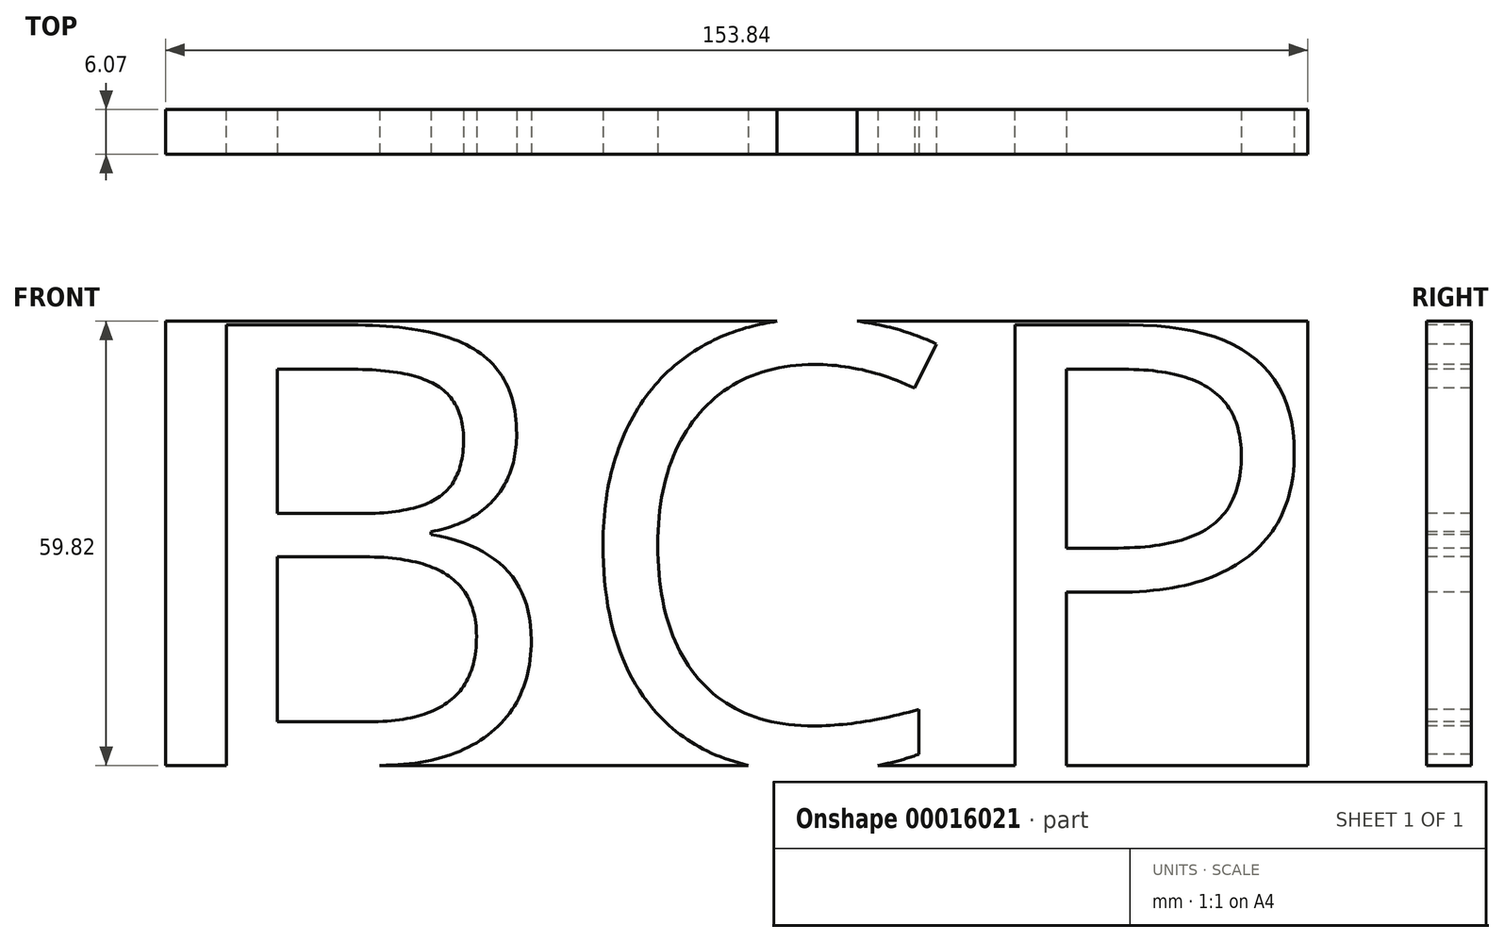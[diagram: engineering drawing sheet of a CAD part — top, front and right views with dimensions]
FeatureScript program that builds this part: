
annotation { "Feature Type Name" : "Feature", "Feature Type Description" : "" }
export const myFeature = defineFeature(function(context is Context, id is Id, definition is map)
    precondition{}
    {
        {
            var Q0;
            Q0=qCreatedBy(makeId("Front.planeOp"),FACE);
            var sketch = newSketch(context, id + "F0", { "sketchPlane" : qUnion([Q0])});
            skLineSegment(sketch, "E0.rect.bottom", {"start": v(76.92, 29.91) * mm, "end": v(-76.92, 29.91) * mm});
            skLineSegment(sketch, "E0.rect.top", {"start": v(76.92, -29.91) * mm, "end": v(-76.92, -29.91) * mm});
            skLineSegment(sketch, "E0.rect.left", {"start": v(76.92, 29.91) * mm, "end": v(76.92, -29.91) * mm});
            skLineSegment(sketch, "E0.rect.right", {"start": v(-76.92, 29.91) * mm, "end": v(-76.92, -29.91) * mm});
            skPoint(sketch, "E0.rect.middle", {"position": v(0, 0) * mm});
            skSolve(sketch);
        }
        {
            var Q0;
            Q0=makeQuery(id+"F0.imprint","IMPRINT",FACE,{"disambiguationData":[TD([[makeQuery(id+"F0.imprint","IMPRINT",EDGE,{"derivedFrom":sQuery(id+"F0.wireOp",EDGE,"E0.rect.bottom")}),1.0]])]});
            extrude(context, id + "F1", {"entities" : qUnion([Q0]), "depth" : 6.07 * mm});
        }
        {
            var Q0;
            Q0=makeQuery(id+"F1.opExtrude","CAP_FACE",FACE,{"disambiguationData":[OSD([sQuery(id+"F0.wireOp",EDGE,"E0.rect.bottom"),sQuery(id+"F0.wireOp",EDGE,"E0.rect.top"),sQuery(id+"F0.wireOp",EDGE,"E0.rect.left"),sQuery(id+"F0.wireOp",EDGE,"E0.rect.right")])],"isStart":false});
            var sketch = newSketch(context, id + "F2", { "sketchPlane" : qUnion([Q0])});
            skText(sketch, "E1", { "text": "BCP", "fontName": "OpenSans-Regular.ttf"});
            const initialGuessF2  = {"E1": [-0.07692, -0.02991, 1, 0, 0.05983]};
            skSetInitialGuess(sketch, initialGuessF2);
            skSolve(sketch);
        }
        {
            var Q0;
            Q0=makeQuery(id+"F2.imprint","IMPRINT",FACE,{"disambiguationData":[TD([[makeQuery(id+"F2.imprint","IMPRINT",EDGE,{"derivedFrom":sQuery(id+"F2.wireOp",EDGE,"E1.sketch_text.stroke-25")}),-1.0]])]});
            var Q1;
            Q1=makeQuery(id+"F2.imprint","IMPRINT",FACE,{"disambiguationData":[TD([[makeQuery(id+"F2.imprint","IMPRINT",EDGE,{"derivedFrom":sQuery(id+"F2.wireOp",EDGE,"E1.sketch_text.stroke-40")}),-1.0]])]});
            var Q2;
            Q2=makeQuery(id+"F2.imprint","IMPRINT",FACE,{"disambiguationData":[TD([[makeQuery(id+"F2.imprint","IMPRINT",EDGE,{"derivedFrom":sQuery(id+"F2.wireOp",EDGE,"E1.sketch_text.stroke-0")}),-1.0]])]});
            extrude(context, id + "F3", {"entities" : qUnion([Q0, Q1, Q2]), "operationType" : NewBodyOperationType.REMOVE, "oppositeDirection" : true, "depth" : 25.4 * mm});
        }
    });
